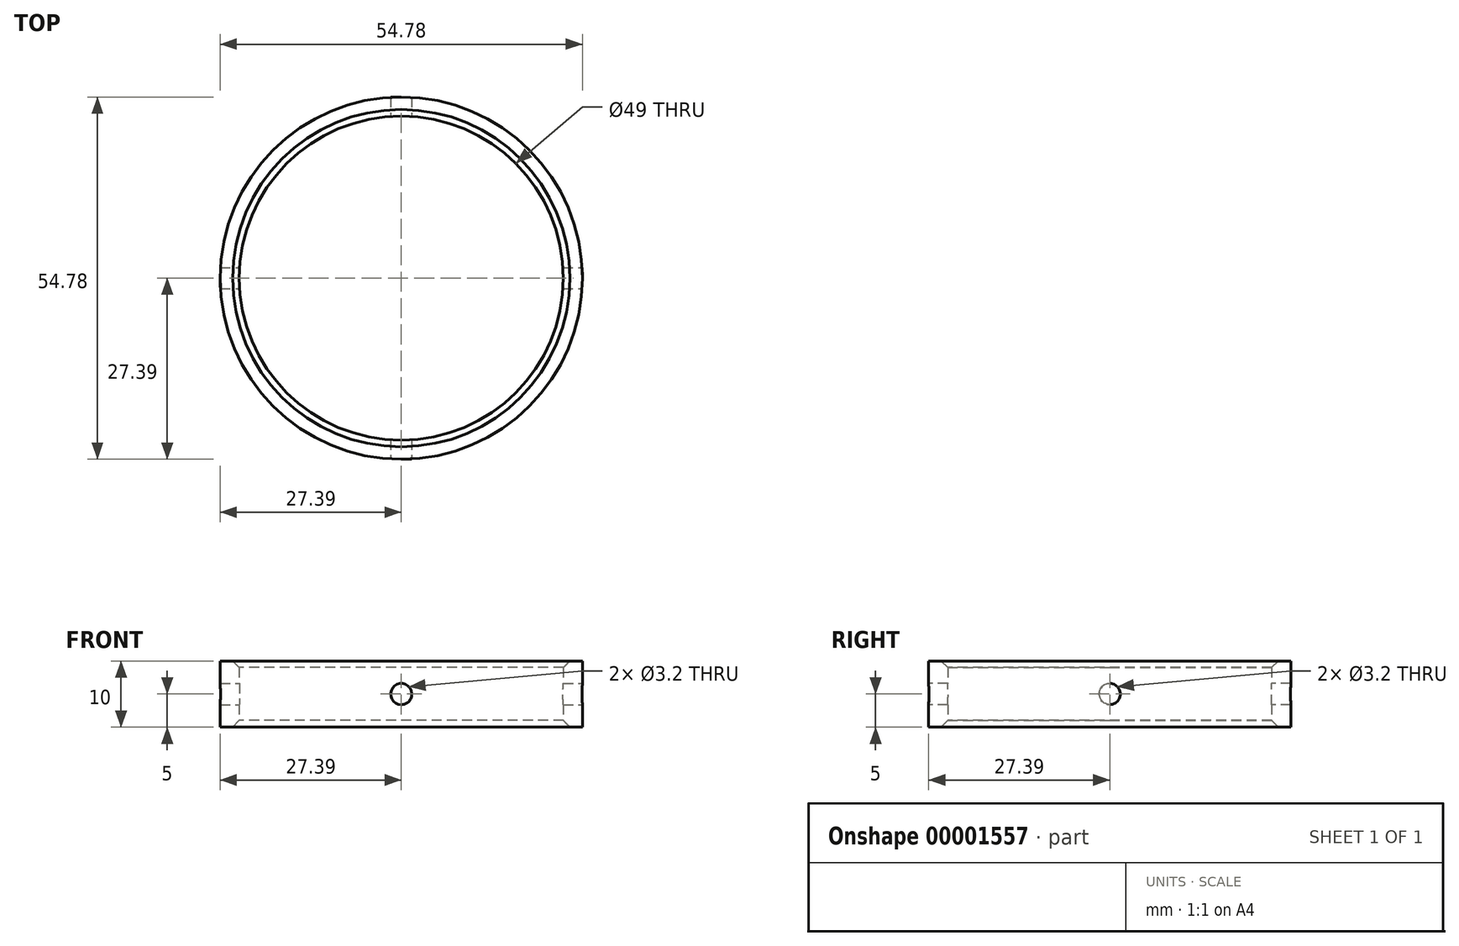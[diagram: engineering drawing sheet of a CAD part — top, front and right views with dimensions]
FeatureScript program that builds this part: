
annotation { "Feature Type Name" : "Feature", "Feature Type Description" : "" }
export const myFeature = defineFeature(function(context is Context, id is Id, definition is map)
    precondition{}
    {
        {
            var Q0;
            Q0=qCreatedBy(makeId("Top.planeOp"),FACE);
            var sketch = newSketch(context, id + "F0", { "sketchPlane" : qUnion([Q0])});
            skCircle(sketch, "E0", {"center": v(0, 0) * mm, "radius": 24.5 * mm});
            skCircle(sketch, "E1", {"center": v(0, 0) * mm, "radius": 35 * mm});
            skCircle(sketch, "E2", {"center": v(0, 0) * mm, "radius": 27.4 * mm});
            skCircle(sketch, "E3.cCircle", {"center": v(0, 0) * mm, "radius": 27.4 * mm, "construction": true});
            skPoint(sketch, "E3.0.midPoint", {"position": v(-27.4, 0) * mm});
            skCircle(sketch, "E4", {"center": v(-27.4, 15.82) * mm, "radius": 1.6 * mm});
            skCircle(sketch, "E5", {"center": v(-27.4, -15.82) * mm, "radius": 1.6 * mm});
            skCircle(sketch, "E6.0.MirrorC", {"center": v(27.4, 15.82) * mm, "radius": 1.6 * mm});
            skCircle(sketch, "E7.0.MirrorC", {"center": v(27.4, -15.82) * mm, "radius": 1.6 * mm});
            skSolve(sketch);
        }
        {
            var Q0;
            Q0=makeQuery(id+"F0.imprint","IMPRINT",FACE,{"disambiguationData":[TD([[makeQuery(id+"F0.imprint","IMPRINT",EDGE,{"derivedFrom":sQuery(id+"F0.wireOp",EDGE,"E0")}),-1.0]])]});
            extrude(context, id + "F1", {"entities" : qUnion([Q0]), "depth" : 10 * mm});
        }
        {
            var Q0;
            Q0=qCreatedBy(makeId("Right.planeOp"),FACE);
            var sketch = newSketch(context, id + "F2", { "sketchPlane" : qUnion([Q0])});
            skCircle(sketch, "E8", {"center": v(0, 5) * mm, "radius": 1.6 * mm});
            skSolve(sketch);
        }
        {
            var Q0;
            Q0=makeQuery(id+"F2.imprint","IMPRINT",FACE,{"disambiguationData":[TD([[makeQuery(id+"F2.imprint","IMPRINT",EDGE,{"derivedFrom":sQuery(id+"F2.wireOp",EDGE,"E8")}),1.0]])]});
            extrude(context, id + "F3", {"entities" : qUnion([Q0]), "operationType" : NewBodyOperationType.REMOVE, "endBound" : BoundingType.SYMMETRIC, "oppositeDirection" : true, "depth" : 80 * mm});
        }
        {
            var Q0;
            Q0=makeQuery(id+"F1.opExtrude","CAP_EDGE",EDGE,{"disambiguationData":[OSD([sQuery(id+"F0.wireOp",EDGE,"E0")])],"isStart":false});
            chamfer(context, id + "F4", {"entities" : qUnion([Q0]), "width" : 1 * mm, "tangentPropagation" : true});
        }
        {
            var Q0;
            Q0=makeQuery(id+"F1.opExtrude","CAP_EDGE",EDGE,{"disambiguationData":[OSD([sQuery(id+"F0.wireOp",EDGE,"E0")])],"isStart":true});
            chamfer(context, id + "F5", {"entities" : qUnion([Q0]), "width" : 1 * mm, "tangentPropagation" : true});
        }
        {
            var Q0;
            Q0=qCreatedBy(makeId("Front.planeOp"),FACE);
            var sketch = newSketch(context, id + "F6", { "sketchPlane" : qUnion([Q0])});
            skCircle(sketch, "E9", {"center": v(0, 5) * mm, "radius": 1.6 * mm});
            skSolve(sketch);
        }
        {
            var Q0;
            Q0=makeQuery(id+"F6.imprint","IMPRINT",FACE,{"disambiguationData":[TD([[makeQuery(id+"F6.imprint","IMPRINT",EDGE,{"derivedFrom":sQuery(id+"F6.wireOp",EDGE,"E9")}),1.0]])]});
            extrude(context, id + "F7", {"entities" : qUnion([Q0]), "operationType" : NewBodyOperationType.REMOVE, "endBound" : BoundingType.SYMMETRIC, "oppositeDirection" : true, "depth" : 57.6 * mm});
        }
    });
